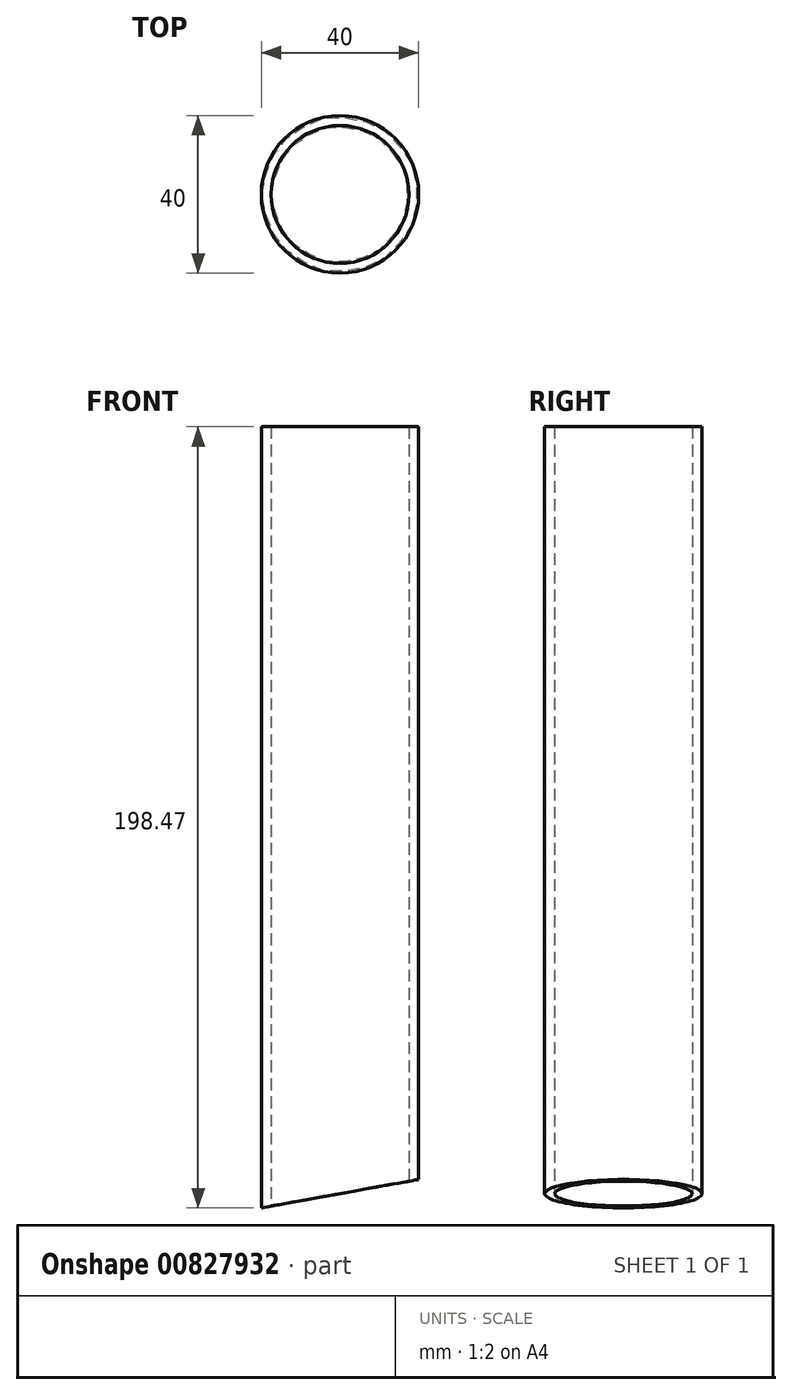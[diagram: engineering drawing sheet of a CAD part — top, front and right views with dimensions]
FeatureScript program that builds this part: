
annotation { "Feature Type Name" : "Feature", "Feature Type Description" : "" }
export const myFeature = defineFeature(function(context is Context, id is Id, definition is map)
    precondition{}
    {
        {
            var Q0;
            Q0=qCreatedBy(makeId("Top.planeOp"),FACE);
            var sketch = newSketch(context, id + "F0", { "sketchPlane" : qUnion([Q0])});
            skCircle(sketch, "E0", {"center": v(0, 0) * mm, "radius": 20 * mm});
            skCircle(sketch, "E1", {"center": v(0, 0) * mm, "radius": 17.5 * mm});
            skSolve(sketch);
        }
        {
            var Q0;
            Q0=makeQuery(id+"F0.imprint","IMPRINT",FACE,{"disambiguationData":[TD([[makeQuery(id+"F0.imprint","IMPRINT",EDGE,{"derivedFrom":sQuery(id+"F0.wireOp",EDGE,"E0")}),1.0]])]});
            extrude(context, id + "F1", {"entities" : qUnion([Q0]), "depth" : (180 + 18 + 0.47) * mm, "offsetDistance" : 25 * mm});
        }
        {
            var Q0;
            Q0=qCreatedBy(makeId("Front.planeOp"),FACE);
            var sketch = newSketch(context, id + "F2", { "sketchPlane" : qUnion([Q0])});
            skLineSegment(sketch, "E2", {"start": v(-20, 0) * mm, "end": v(0, 0) * mm});
            skLineSegment(sketch, "E3", {"start": v(0, 0) * mm, "end": v(20, 0) * mm});
            skLineSegment(sketch, "E4", {"start": v(20, 0) * mm, "end": v(20, 19.08) * mm});
            skLineSegment(sketch, "E5", {"start": v(-20, 0) * mm, "end": v(20, 7.2) * mm});
            skSolve(sketch);
        }
        {
            var Q0;
            Q0=qSketchRegion(id+"F2",true);
            extrude(context, id + "F3", {"entities" : qUnion([Q0]), "operationType" : NewBodyOperationType.REMOVE, "endBound" : BoundingType.SYMMETRIC, "oppositeDirection" : true, "depth" : 50 * mm, "offsetDistance" : 25 * mm});
        }
    });
